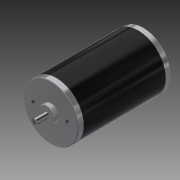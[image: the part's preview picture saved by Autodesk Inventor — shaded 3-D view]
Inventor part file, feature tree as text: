
AUTODESK INVENTOR PART (.ipt)
format: ipt  version: 2018 (Build 220112000, 112)  size: 126,464 bytes
history: native  units: in
note: dims shown in document units (in); Inventor stores cm internally (conversion verified against a paired STEP export)
features: thread x2, chamfer x1, other x1, imported_body x1
ambient origin geometry x8: Origin, YZ Plane, XZ Plane, XY Plane, X Axis, Y Axis, Z Axis, Center Point
bodies: Body1 (feature_tree)
feature tree (5):
  chamfer  "Chamfer1"  Distance=0.3937in
  other  "217-3351-STEP1"
  thread  "Thread1"  [1 undecoded]
  thread  "Thread2"  [1 undecoded]
  imported_body  "Base1"
note: 2 required parameter values undecoded (feature->parameter linkage not recoverable at this tier; creation-order binding heuristic only, values carry confidence <= 0.55)
